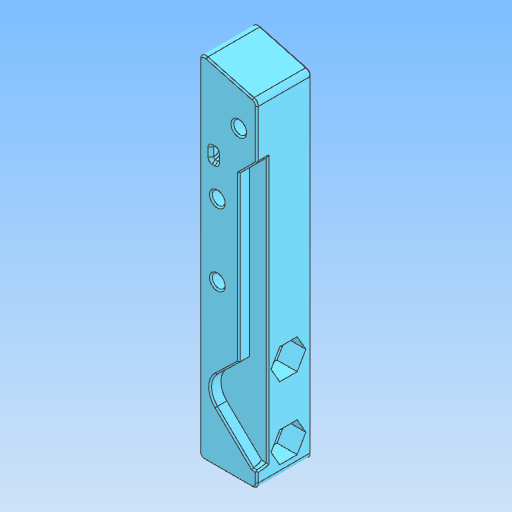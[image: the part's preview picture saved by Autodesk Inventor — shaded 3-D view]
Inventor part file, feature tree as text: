
AUTODESK INVENTOR PART (.ipt)
format: ipt  version: 2021.2 (Build 252289000, 289)  size: 384,512 bytes
history: native  units: mm
features: other x4, chamfer x4, fillet x3
ambient origin geometry x8: Origin, YZ Plane, XZ Plane, XY Plane, X Axis, Y Axis, Z Axis, Center Point
bodies: Body1 (feature_tree)
feature tree (11):
  other  "Твёрдое тело.ipt"
  fillet  "Сопряжение1"  Radius=10.0mm
  chamfer  "Фаска1"  Distance=2.0mm
  chamfer  "Фаска2"  Distance=0.5mm Angle=45.0deg
  chamfer  "Фаска3"  Distance=0.5mm Angle=45.0deg
  fillet  "Сопряжение3"  Radius=0.5mm
  fillet  "Сопряжение2"  Radius=0.5mm
  chamfer  "Фаска4"  Distance=1.0mm Angle=45.0deg
  other  "Ножка левая низ::Твёрдое тело.ipt"
  other  "Элемент создания тегов1"
  other  "Твердое тело1"
